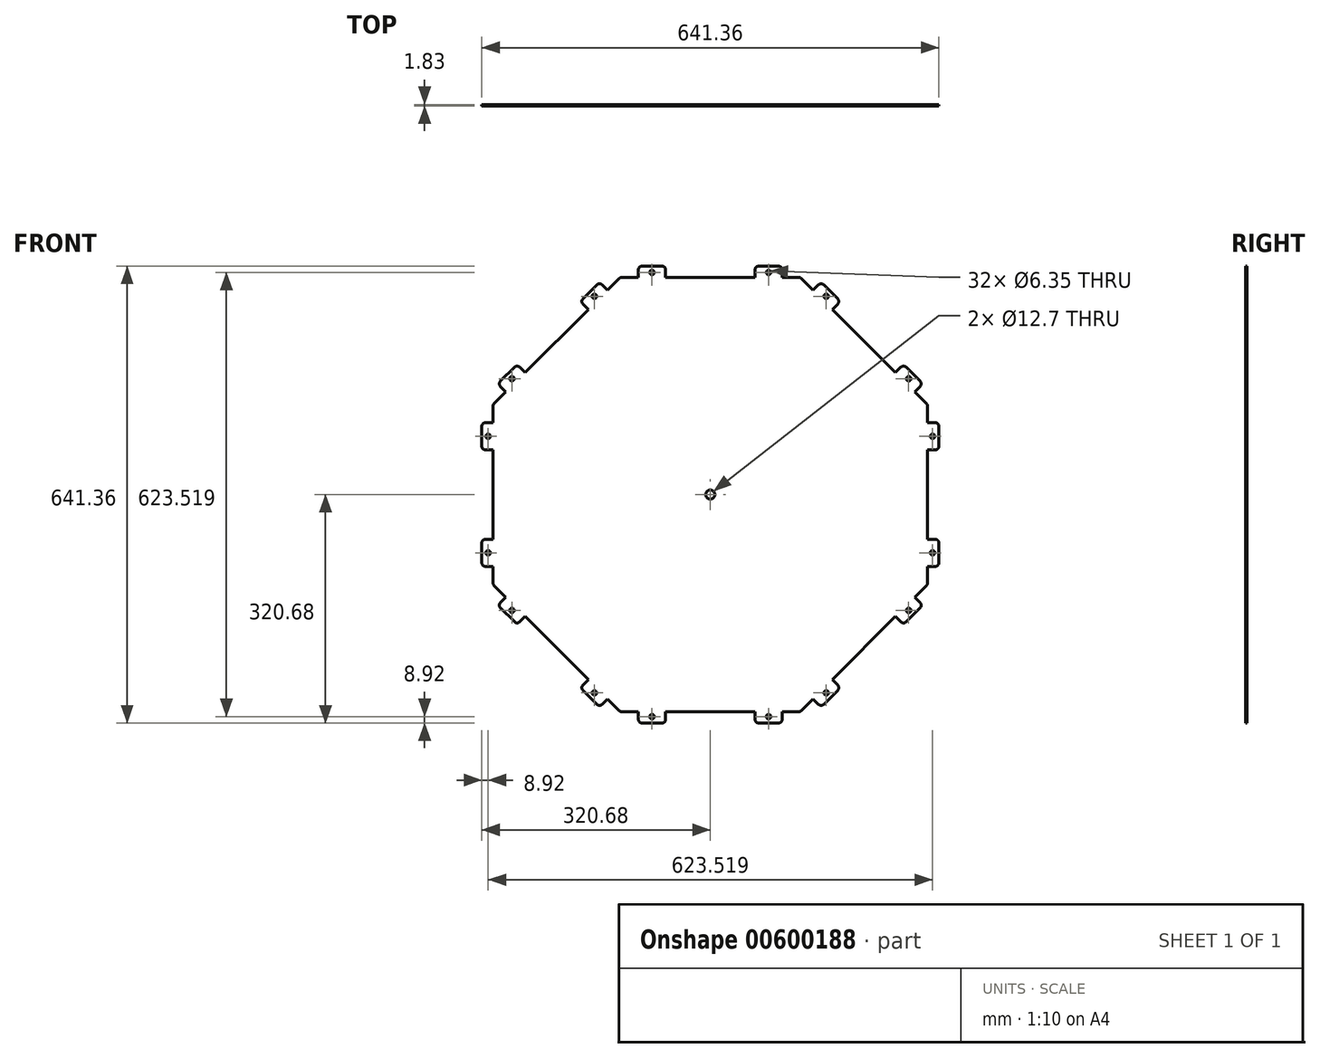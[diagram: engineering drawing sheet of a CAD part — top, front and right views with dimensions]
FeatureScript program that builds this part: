
annotation { "Feature Type Name" : "Feature", "Feature Type Description" : "" }
export const myFeature = defineFeature(function(context is Context, id is Id, definition is map)
    precondition{}
    {
        {
            var Q0;
            Q0=qCreatedBy(makeId("Front.planeOp"),FACE);
            var sketch = newSketch(context, id + "F0", { "sketchPlane" : qUnion([Q0])});
            skLineSegment(sketch, "E0.bottom", {"start": v(-126.24, 304.8) * mm, "end": v(-100.84, 304.8) * mm});
            skLineSegment(sketch, "E0.top", {"start": v(-126.24, -304.8) * mm, "end": v(-100.84, -304.8) * mm});
            skLineSegment(sketch, "E0.left", {"start": v(-304.8, 126.24) * mm, "end": v(-304.8, 100.84) * mm});
            skLineSegment(sketch, "E0.right", {"start": v(304.8, 126.24) * mm, "end": v(304.8, 100.84) * mm});
            skLineSegment(sketch, "E1", {"start": v(-126.24, 304.8) * mm, "end": v(-144.22, 286.82) * mm});
            skLineSegment(sketch, "E2", {"start": v(-304.8, -126.24) * mm, "end": v(-286.82, -144.22) * mm});
            skLineSegment(sketch, "E3", {"start": v(126.24, -304.8) * mm, "end": v(144.22, -286.82) * mm});
            skLineSegment(sketch, "E4", {"start": v(126.24, 304.8) * mm, "end": v(144.22, 286.82) * mm});
            skPoint(sketch, "E5.orphan", {"position": v(-304.8, 304.8) * mm});
            skPoint(sketch, "E6.orphan", {"position": v(304.8, 304.8) * mm});
            skPoint(sketch, "E7.orphan", {"position": v(304.8, -304.8) * mm});
            skPoint(sketch, "E8.orphan", {"position": v(-304.8, -304.8) * mm});
            skLineSegment(sketch, "E9", {"start": v(-126.24, -304.8) * mm, "end": v(126.24, 304.8) * mm, "construction": true});
            skLineSegment(sketch, "E10", {"start": v(-304.8, 126.24) * mm, "end": v(304.8, -126.24) * mm, "construction": true});
            skLineSegment(sketch, "E11", {"start": v(-100.84, 304.8) * mm, "end": v(-100.84, 320.67) * mm});
            skLineSegment(sketch, "E12", {"start": v(-100.84, 320.67) * mm, "end": v(-62.74, 320.67) * mm});
            skLineSegment(sketch, "E13", {"start": v(-62.74, 320.67) * mm, "end": v(-62.74, 304.8) * mm});
            skLineSegment(sketch, "E14", {"start": v(62.74, 304.8) * mm, "end": v(62.74, 320.67) * mm});
            skLineSegment(sketch, "E15", {"start": v(62.74, 320.67) * mm, "end": v(100.84, 320.67) * mm});
            skLineSegment(sketch, "E16", {"start": v(100.84, 320.67) * mm, "end": v(100.84, 304.8) * mm});
            skLineSegment(sketch, "E17.1.0", {"start": v(-171.16, 259.88) * mm, "end": v(-182.39, 271.11) * mm});
            skLineSegment(sketch, "E17.1.1", {"start": v(-182.39, 271.11) * mm, "end": v(-155.45, 298.05) * mm});
            skLineSegment(sketch, "E17.1.2", {"start": v(-271.11, 182.39) * mm, "end": v(-259.88, 171.16) * mm});
            skLineSegment(sketch, "E17.1.3", {"start": v(-155.45, 298.05) * mm, "end": v(-144.22, 286.82) * mm});
            skLineSegment(sketch, "E17.1.4", {"start": v(-286.82, 144.22) * mm, "end": v(-298.05, 155.45) * mm});
            skLineSegment(sketch, "E17.1.5", {"start": v(-298.05, 155.45) * mm, "end": v(-271.11, 182.39) * mm});
            skLineSegment(sketch, "E17.2.0", {"start": v(-304.8, 62.74) * mm, "end": v(-320.68, 62.74) * mm});
            skLineSegment(sketch, "E17.2.1", {"start": v(-320.68, 62.74) * mm, "end": v(-320.68, 100.84) * mm});
            skLineSegment(sketch, "E17.2.2", {"start": v(-320.68, -62.74) * mm, "end": v(-304.8, -62.74) * mm});
            skLineSegment(sketch, "E17.2.3", {"start": v(-320.68, 100.84) * mm, "end": v(-304.8, 100.84) * mm});
            skLineSegment(sketch, "E17.2.4", {"start": v(-304.8, -100.84) * mm, "end": v(-320.68, -100.84) * mm});
            skLineSegment(sketch, "E17.2.5", {"start": v(-320.68, -100.84) * mm, "end": v(-320.68, -62.74) * mm});
            skPoint(sketch, "E17.center", {"position": v(0, 0) * mm});
            skCircle(sketch, "E18", {"center": v(-81.79, 311.76) * mm, "radius": 3.18 * mm});
            skCircle(sketch, "E19", {"center": v(81.79, 311.76) * mm, "radius": 3.18 * mm});
            skLineSegment(sketch, "E20.3.3.0", {"start": v(-271.11, -182.39) * mm, "end": v(-298.05, -155.45) * mm});
            skLineSegment(sketch, "E20.6.3.0", {"start": v(-182.39, -271.11) * mm, "end": v(-171.16, -259.88) * mm});
            skLineSegment(sketch, "E20.9.3.0", {"start": v(-298.05, -155.45) * mm, "end": v(-286.82, -144.22) * mm});
            skLineSegment(sketch, "E20.12.3.0", {"start": v(-144.22, -286.82) * mm, "end": v(-155.45, -298.05) * mm});
            skLineSegment(sketch, "E20.13.3.0", {"start": v(-259.88, -171.16) * mm, "end": v(-271.11, -182.39) * mm});
            skLineSegment(sketch, "E20.15.3.0", {"start": v(-155.45, -298.05) * mm, "end": v(-182.39, -271.11) * mm});
            skLineSegment(sketch, "E20.3.4.0", {"start": v(-62.74, -320.67) * mm, "end": v(-100.84, -320.67) * mm});
            skLineSegment(sketch, "E20.6.4.0", {"start": v(62.74, -320.67) * mm, "end": v(62.74, -304.8) * mm});
            skLineSegment(sketch, "E20.9.4.0", {"start": v(-100.84, -320.67) * mm, "end": v(-100.84, -304.8) * mm});
            skLineSegment(sketch, "E20.12.4.0", {"start": v(100.84, -304.8) * mm, "end": v(100.84, -320.67) * mm});
            skLineSegment(sketch, "E20.13.4.0", {"start": v(-62.74, -304.8) * mm, "end": v(-62.74, -320.67) * mm});
            skLineSegment(sketch, "E20.15.4.0", {"start": v(100.84, -320.67) * mm, "end": v(62.74, -320.67) * mm});
            skLineSegment(sketch, "E20.3.5.0", {"start": v(182.39, -271.11) * mm, "end": v(155.45, -298.05) * mm});
            skLineSegment(sketch, "E20.6.5.0", {"start": v(271.11, -182.39) * mm, "end": v(259.88, -171.16) * mm});
            skLineSegment(sketch, "E20.9.5.0", {"start": v(155.45, -298.05) * mm, "end": v(144.22, -286.82) * mm});
            skLineSegment(sketch, "E20.12.5.0", {"start": v(286.82, -144.22) * mm, "end": v(298.05, -155.45) * mm});
            skLineSegment(sketch, "E20.13.5.0", {"start": v(171.16, -259.88) * mm, "end": v(182.39, -271.11) * mm});
            skLineSegment(sketch, "E20.15.5.0", {"start": v(298.05, -155.45) * mm, "end": v(271.11, -182.39) * mm});
            skLineSegment(sketch, "E20.3.6.0", {"start": v(320.67, -62.74) * mm, "end": v(320.67, -100.84) * mm});
            skLineSegment(sketch, "E20.6.6.0", {"start": v(320.67, 62.74) * mm, "end": v(304.8, 62.74) * mm});
            skLineSegment(sketch, "E20.9.6.0", {"start": v(320.67, -100.84) * mm, "end": v(304.8, -100.84) * mm});
            skLineSegment(sketch, "E20.12.6.0", {"start": v(304.8, 100.84) * mm, "end": v(320.67, 100.84) * mm});
            skLineSegment(sketch, "E20.13.6.0", {"start": v(304.8, -62.74) * mm, "end": v(320.67, -62.74) * mm});
            skLineSegment(sketch, "E20.15.6.0", {"start": v(320.67, 100.84) * mm, "end": v(320.67, 62.74) * mm});
            skLineSegment(sketch, "E20.3.7.0", {"start": v(271.11, 182.39) * mm, "end": v(298.05, 155.45) * mm});
            skLineSegment(sketch, "E20.6.7.0", {"start": v(182.39, 271.11) * mm, "end": v(171.16, 259.88) * mm});
            skLineSegment(sketch, "E20.9.7.0", {"start": v(298.05, 155.45) * mm, "end": v(286.82, 144.22) * mm});
            skLineSegment(sketch, "E20.12.7.0", {"start": v(144.22, 286.82) * mm, "end": v(155.45, 298.05) * mm});
            skLineSegment(sketch, "E20.13.7.0", {"start": v(259.88, 171.16) * mm, "end": v(271.11, 182.39) * mm});
            skLineSegment(sketch, "E20.15.7.0", {"start": v(155.45, 298.05) * mm, "end": v(182.39, 271.11) * mm});
            skPoint(sketch, "E21.orphan", {"position": v(-259.89, 171.16) * mm});
            skPoint(sketch, "E22.orphan", {"position": v(-286.83, 144.22) * mm});
            skPoint(sketch, "E23.orphan", {"position": v(-144.22, 286.83) * mm});
            skPoint(sketch, "E24.orphan", {"position": v(-171.16, 259.89) * mm});
            skPoint(sketch, "E25.orphan", {"position": v(144.22, 286.83) * mm});
            skPoint(sketch, "E26.orphan", {"position": v(171.16, 259.89) * mm});
            skPoint(sketch, "E27.orphan", {"position": v(259.89, 171.16) * mm});
            skPoint(sketch, "E28.orphan", {"position": v(286.83, 144.22) * mm});
            skPoint(sketch, "E29.orphan", {"position": v(286.83, -144.22) * mm});
            skPoint(sketch, "E30.orphan", {"position": v(259.89, -171.16) * mm});
            skPoint(sketch, "E31.orphan", {"position": v(171.16, -259.89) * mm});
            skPoint(sketch, "E32.orphan", {"position": v(144.22, -286.83) * mm});
            skPoint(sketch, "E33.orphan", {"position": v(-144.22, -286.83) * mm});
            skPoint(sketch, "E34.orphan", {"position": v(-171.16, -259.89) * mm});
            skPoint(sketch, "E35.orphan", {"position": v(-259.89, -171.16) * mm});
            skPoint(sketch, "E36.orphan", {"position": v(-286.83, -144.22) * mm});
            skLineSegment(sketch, "E37.trimOffspring", {"start": v(-62.74, 304.8) * mm, "end": v(62.74, 304.8) * mm});
            skLineSegment(sketch, "E38.trimOffspring", {"start": v(-171.16, 259.88) * mm, "end": v(-259.88, 171.16) * mm});
            skLineSegment(sketch, "E39.trimOffspring", {"start": v(-286.82, 144.22) * mm, "end": v(-304.8, 126.24) * mm});
            skLineSegment(sketch, "E40.trimOffspring", {"start": v(-304.8, 62.74) * mm, "end": v(-304.8, -62.74) * mm});
            skLineSegment(sketch, "E41.trimOffspring", {"start": v(-304.8, -100.84) * mm, "end": v(-304.8, -126.24) * mm});
            skLineSegment(sketch, "E42.trimOffspring", {"start": v(-259.88, -171.16) * mm, "end": v(-171.16, -259.88) * mm});
            skLineSegment(sketch, "E43.trimOffspring", {"start": v(-144.22, -286.82) * mm, "end": v(-126.24, -304.8) * mm});
            skLineSegment(sketch, "E44.trimOffspring", {"start": v(-62.74, -304.8) * mm, "end": v(62.74, -304.8) * mm});
            skLineSegment(sketch, "E45.trimOffspring", {"start": v(100.84, -304.8) * mm, "end": v(126.24, -304.8) * mm});
            skLineSegment(sketch, "E46.trimOffspring", {"start": v(171.16, -259.88) * mm, "end": v(259.88, -171.16) * mm});
            skLineSegment(sketch, "E47.trimOffspring", {"start": v(286.82, -144.22) * mm, "end": v(304.8, -126.24) * mm});
            skLineSegment(sketch, "E48.trimOffspring", {"start": v(304.8, -100.84) * mm, "end": v(304.8, -126.24) * mm});
            skLineSegment(sketch, "E49.trimOffspring", {"start": v(304.8, 62.74) * mm, "end": v(304.8, -62.74) * mm});
            skLineSegment(sketch, "E50.trimOffspring", {"start": v(286.82, 144.22) * mm, "end": v(304.8, 126.24) * mm});
            skLineSegment(sketch, "E51.trimOffspring", {"start": v(100.84, 304.8) * mm, "end": v(126.24, 304.8) * mm});
            skLineSegment(sketch, "E52.trimOffspring", {"start": v(171.16, 259.88) * mm, "end": v(259.88, 171.16) * mm});
            skCircle(sketch, "E53.1.0", {"center": v(-278.28, 162.61) * mm, "radius": 3.18 * mm});
            skCircle(sketch, "E53.1.1", {"center": v(-162.61, 278.28) * mm, "radius": 3.18 * mm});
            skCircle(sketch, "E53.2.0", {"center": v(-311.76, -81.79) * mm, "radius": 3.18 * mm});
            skCircle(sketch, "E53.2.1", {"center": v(-311.76, 81.79) * mm, "radius": 3.18 * mm});
            skCircle(sketch, "E53.3.0", {"center": v(-162.61, -278.28) * mm, "radius": 3.18 * mm});
            skCircle(sketch, "E53.3.1", {"center": v(-278.28, -162.61) * mm, "radius": 3.18 * mm});
            skCircle(sketch, "E53.4.0", {"center": v(81.79, -311.76) * mm, "radius": 3.18 * mm});
            skCircle(sketch, "E53.4.1", {"center": v(-81.79, -311.76) * mm, "radius": 3.18 * mm});
            skCircle(sketch, "E53.5.0", {"center": v(278.28, -162.61) * mm, "radius": 3.18 * mm});
            skCircle(sketch, "E53.5.1", {"center": v(162.61, -278.28) * mm, "radius": 3.18 * mm});
            skCircle(sketch, "E53.6.0", {"center": v(311.76, 81.79) * mm, "radius": 3.18 * mm});
            skCircle(sketch, "E53.6.1", {"center": v(311.76, -81.79) * mm, "radius": 3.18 * mm});
            skCircle(sketch, "E53.7.0", {"center": v(162.61, 278.28) * mm, "radius": 3.18 * mm});
            skCircle(sketch, "E53.7.1", {"center": v(278.28, 162.61) * mm, "radius": 3.18 * mm});
            skCircle(sketch, "E54", {"center": v(0, 0) * mm, "radius": 6.35 * mm});
            skSolve(sketch);
        }
        {
            var Q0;
            Q0=makeQuery(id+"F0.imprint","IMPRINT",FACE,{"disambiguationData":[TD([[makeQuery(id+"F0.imprint","IMPRINT",EDGE,{"derivedFrom":sQuery(id+"F0.wireOp",EDGE,"E0.bottom")}),-1.0]])]});
            extrude(context, id + "F1", {"entities" : qUnion([Q0]), "depth" : 1.83 * mm, "offsetDistance" : 25.4 * mm});
        }
        {
            var Q0;
            Q0=makeQuery(id+"F1.opExtrude","SWEPT_EDGE",EDGE,{"disambiguationData":[OSD([sQuery(id+"F0.wireOp",EDGE,"E17.1.2"),sQuery(id+"F0.wireOp",EDGE,"E17.1.5")])]});
            var Q1;
            Q1=makeQuery(id+"F1.opExtrude","SWEPT_EDGE",EDGE,{"disambiguationData":[OSD([sQuery(id+"F0.wireOp",EDGE,"E17.1.4"),sQuery(id+"F0.wireOp",EDGE,"E17.1.5")])]});
            var Q2;
            Q2=makeQuery(id+"F1.opExtrude","SWEPT_EDGE",EDGE,{"disambiguationData":[OSD([sQuery(id+"F0.wireOp",EDGE,"E17.1.0"),sQuery(id+"F0.wireOp",EDGE,"E17.1.1")])]});
            var Q3;
            Q3=makeQuery(id+"F1.opExtrude","SWEPT_EDGE",EDGE,{"disambiguationData":[OSD([sQuery(id+"F0.wireOp",EDGE,"E17.1.1"),sQuery(id+"F0.wireOp",EDGE,"E17.1.3")])]});
            var Q4;
            Q4=makeQuery(id+"F1.opExtrude","SWEPT_EDGE",EDGE,{"disambiguationData":[OSD([sQuery(id+"F0.wireOp",EDGE,"E11"),sQuery(id+"F0.wireOp",EDGE,"E12")])]});
            var Q5;
            Q5=makeQuery(id+"F1.opExtrude","SWEPT_EDGE",EDGE,{"disambiguationData":[OSD([sQuery(id+"F0.wireOp",EDGE,"E12"),sQuery(id+"F0.wireOp",EDGE,"E13")])]});
            var Q6;
            Q6=makeQuery(id+"F1.opExtrude","SWEPT_EDGE",EDGE,{"disambiguationData":[OSD([sQuery(id+"F0.wireOp",EDGE,"E14"),sQuery(id+"F0.wireOp",EDGE,"E15")])]});
            var Q7;
            Q7=makeQuery(id+"F1.opExtrude","SWEPT_EDGE",EDGE,{"disambiguationData":[OSD([sQuery(id+"F0.wireOp",EDGE,"E15"),sQuery(id+"F0.wireOp",EDGE,"E16")])]});
            var Q8;
            Q8=makeQuery(id+"F1.opExtrude","SWEPT_EDGE",EDGE,{"disambiguationData":[OSD([sQuery(id+"F0.wireOp",EDGE,"E20.12.7.0"),sQuery(id+"F0.wireOp",EDGE,"E20.15.7.0")])]});
            var Q9;
            Q9=makeQuery(id+"F1.opExtrude","SWEPT_EDGE",EDGE,{"disambiguationData":[OSD([sQuery(id+"F0.wireOp",EDGE,"E20.6.7.0"),sQuery(id+"F0.wireOp",EDGE,"E20.15.7.0")])]});
            var Q10;
            Q10=makeQuery(id+"F1.opExtrude","SWEPT_EDGE",EDGE,{"disambiguationData":[OSD([sQuery(id+"F0.wireOp",EDGE,"E20.3.7.0"),sQuery(id+"F0.wireOp",EDGE,"E20.13.7.0")])]});
            var Q11;
            Q11=makeQuery(id+"F1.opExtrude","SWEPT_EDGE",EDGE,{"disambiguationData":[OSD([sQuery(id+"F0.wireOp",EDGE,"E20.3.7.0"),sQuery(id+"F0.wireOp",EDGE,"E20.9.7.0")])]});
            var Q12;
            Q12=makeQuery(id+"F1.opExtrude","SWEPT_EDGE",EDGE,{"disambiguationData":[OSD([sQuery(id+"F0.wireOp",EDGE,"E20.12.6.0"),sQuery(id+"F0.wireOp",EDGE,"E20.15.6.0")])]});
            var Q13;
            Q13=makeQuery(id+"F1.opExtrude","SWEPT_EDGE",EDGE,{"disambiguationData":[OSD([sQuery(id+"F0.wireOp",EDGE,"E20.6.6.0"),sQuery(id+"F0.wireOp",EDGE,"E20.15.6.0")])]});
            var Q14;
            Q14=makeQuery(id+"F1.opExtrude","SWEPT_EDGE",EDGE,{"disambiguationData":[OSD([sQuery(id+"F0.wireOp",EDGE,"E20.3.6.0"),sQuery(id+"F0.wireOp",EDGE,"E20.13.6.0")])]});
            var Q15;
            Q15=makeQuery(id+"F1.opExtrude","SWEPT_EDGE",EDGE,{"disambiguationData":[OSD([sQuery(id+"F0.wireOp",EDGE,"E20.3.6.0"),sQuery(id+"F0.wireOp",EDGE,"E20.9.6.0")])]});
            var Q16;
            Q16=makeQuery(id+"F1.opExtrude","SWEPT_EDGE",EDGE,{"disambiguationData":[OSD([sQuery(id+"F0.wireOp",EDGE,"E20.12.5.0"),sQuery(id+"F0.wireOp",EDGE,"E20.15.5.0")])]});
            var Q17;
            Q17=makeQuery(id+"F1.opExtrude","SWEPT_EDGE",EDGE,{"disambiguationData":[OSD([sQuery(id+"F0.wireOp",EDGE,"E20.6.5.0"),sQuery(id+"F0.wireOp",EDGE,"E20.15.5.0")])]});
            var Q18;
            Q18=makeQuery(id+"F1.opExtrude","SWEPT_EDGE",EDGE,{"disambiguationData":[OSD([sQuery(id+"F0.wireOp",EDGE,"E20.3.5.0"),sQuery(id+"F0.wireOp",EDGE,"E20.13.5.0")])]});
            var Q19;
            Q19=makeQuery(id+"F1.opExtrude","SWEPT_EDGE",EDGE,{"disambiguationData":[OSD([sQuery(id+"F0.wireOp",EDGE,"E20.3.5.0"),sQuery(id+"F0.wireOp",EDGE,"E20.9.5.0")])]});
            var Q20;
            Q20=makeQuery(id+"F1.opExtrude","SWEPT_EDGE",EDGE,{"disambiguationData":[OSD([sQuery(id+"F0.wireOp",EDGE,"E20.12.4.0"),sQuery(id+"F0.wireOp",EDGE,"E20.15.4.0")])]});
            var Q21;
            Q21=makeQuery(id+"F1.opExtrude","SWEPT_EDGE",EDGE,{"disambiguationData":[OSD([sQuery(id+"F0.wireOp",EDGE,"E20.6.4.0"),sQuery(id+"F0.wireOp",EDGE,"E20.15.4.0")])]});
            var Q22;
            Q22=makeQuery(id+"F1.opExtrude","SWEPT_EDGE",EDGE,{"disambiguationData":[OSD([sQuery(id+"F0.wireOp",EDGE,"E20.3.4.0"),sQuery(id+"F0.wireOp",EDGE,"E20.13.4.0")])]});
            var Q23;
            Q23=makeQuery(id+"F1.opExtrude","SWEPT_EDGE",EDGE,{"disambiguationData":[OSD([sQuery(id+"F0.wireOp",EDGE,"E20.3.4.0"),sQuery(id+"F0.wireOp",EDGE,"E20.9.4.0")])]});
            var Q24;
            Q24=makeQuery(id+"F1.opExtrude","SWEPT_EDGE",EDGE,{"disambiguationData":[OSD([sQuery(id+"F0.wireOp",EDGE,"E20.12.3.0"),sQuery(id+"F0.wireOp",EDGE,"E20.15.3.0")])]});
            var Q25;
            Q25=makeQuery(id+"F1.opExtrude","SWEPT_EDGE",EDGE,{"disambiguationData":[OSD([sQuery(id+"F0.wireOp",EDGE,"E20.6.3.0"),sQuery(id+"F0.wireOp",EDGE,"E20.15.3.0")])]});
            var Q26;
            Q26=makeQuery(id+"F1.opExtrude","SWEPT_EDGE",EDGE,{"disambiguationData":[OSD([sQuery(id+"F0.wireOp",EDGE,"E20.3.3.0"),sQuery(id+"F0.wireOp",EDGE,"E20.13.3.0")])]});
            var Q27;
            Q27=makeQuery(id+"F1.opExtrude","SWEPT_EDGE",EDGE,{"disambiguationData":[OSD([sQuery(id+"F0.wireOp",EDGE,"E20.3.3.0"),sQuery(id+"F0.wireOp",EDGE,"E20.9.3.0")])]});
            var Q28;
            Q28=makeQuery(id+"F1.opExtrude","SWEPT_EDGE",EDGE,{"disambiguationData":[OSD([sQuery(id+"F0.wireOp",EDGE,"E17.2.4"),sQuery(id+"F0.wireOp",EDGE,"E17.2.5")])]});
            var Q29;
            Q29=makeQuery(id+"F1.opExtrude","SWEPT_EDGE",EDGE,{"disambiguationData":[OSD([sQuery(id+"F0.wireOp",EDGE,"E17.2.2"),sQuery(id+"F0.wireOp",EDGE,"E17.2.5")])]});
            var Q30;
            Q30=makeQuery(id+"F1.opExtrude","SWEPT_EDGE",EDGE,{"disambiguationData":[OSD([sQuery(id+"F0.wireOp",EDGE,"E17.2.0"),sQuery(id+"F0.wireOp",EDGE,"E17.2.1")])]});
            var Q31;
            Q31=makeQuery(id+"F1.opExtrude","SWEPT_EDGE",EDGE,{"disambiguationData":[OSD([sQuery(id+"F0.wireOp",EDGE,"E17.2.1"),sQuery(id+"F0.wireOp",EDGE,"E17.2.3")])]});
            var Q32;
            Q32=makeQuery(id+"F1.opExtrude","SWEPT_EDGE",EDGE,{"disambiguationData":[OSD([sQuery(id+"F0.wireOp",EDGE,"E4"),sQuery(id+"F0.wireOp",EDGE,"E51.trimOffspring")])]});
            var Q33;
            Q33=makeQuery(id+"F1.opExtrude","SWEPT_EDGE",EDGE,{"disambiguationData":[OSD([sQuery(id+"F0.wireOp",EDGE,"E0.right"),sQuery(id+"F0.wireOp",EDGE,"E50.trimOffspring")])]});
            var Q34;
            Q34=makeQuery(id+"F1.opExtrude","SWEPT_EDGE",EDGE,{"disambiguationData":[OSD([sQuery(id+"F0.wireOp",EDGE,"E47.trimOffspring"),sQuery(id+"F0.wireOp",EDGE,"E48.trimOffspring")])]});
            var Q35;
            Q35=makeQuery(id+"F1.opExtrude","SWEPT_EDGE",EDGE,{"disambiguationData":[OSD([sQuery(id+"F0.wireOp",EDGE,"E3"),sQuery(id+"F0.wireOp",EDGE,"E45.trimOffspring")])]});
            var Q36;
            Q36=makeQuery(id+"F1.opExtrude","SWEPT_EDGE",EDGE,{"disambiguationData":[OSD([sQuery(id+"F0.wireOp",EDGE,"E0.top"),sQuery(id+"F0.wireOp",EDGE,"E43.trimOffspring")])]});
            var Q37;
            Q37=makeQuery(id+"F1.opExtrude","SWEPT_EDGE",EDGE,{"disambiguationData":[OSD([sQuery(id+"F0.wireOp",EDGE,"E2"),sQuery(id+"F0.wireOp",EDGE,"E41.trimOffspring")])]});
            var Q38;
            Q38=makeQuery(id+"F1.opExtrude","SWEPT_EDGE",EDGE,{"disambiguationData":[OSD([sQuery(id+"F0.wireOp",EDGE,"E0.left"),sQuery(id+"F0.wireOp",EDGE,"E39.trimOffspring")])]});
            var Q39;
            Q39=makeQuery(id+"F1.opExtrude","SWEPT_EDGE",EDGE,{"disambiguationData":[OSD([sQuery(id+"F0.wireOp",EDGE,"E0.bottom"),sQuery(id+"F0.wireOp",EDGE,"E1")])]});
            fillet(context, id + "F2", {"entities" : qUnion([Q0, Q1, Q2, Q3, Q4, Q5, Q6, Q7, Q8, Q9, Q10, Q11, Q12, Q13, Q14, Q15, Q16, Q17, Q18, Q19, Q20, Q21, Q22, Q23, Q24, Q25, Q26, Q27, Q28, Q29, Q30, Q31, Q32, Q33, Q34, Q35, Q36, Q37, Q38, Q39]), "radius" : 5.08 * mm, "tangentPropagation" : true, "allowEdgeOverflow" : false});
        }
    });
